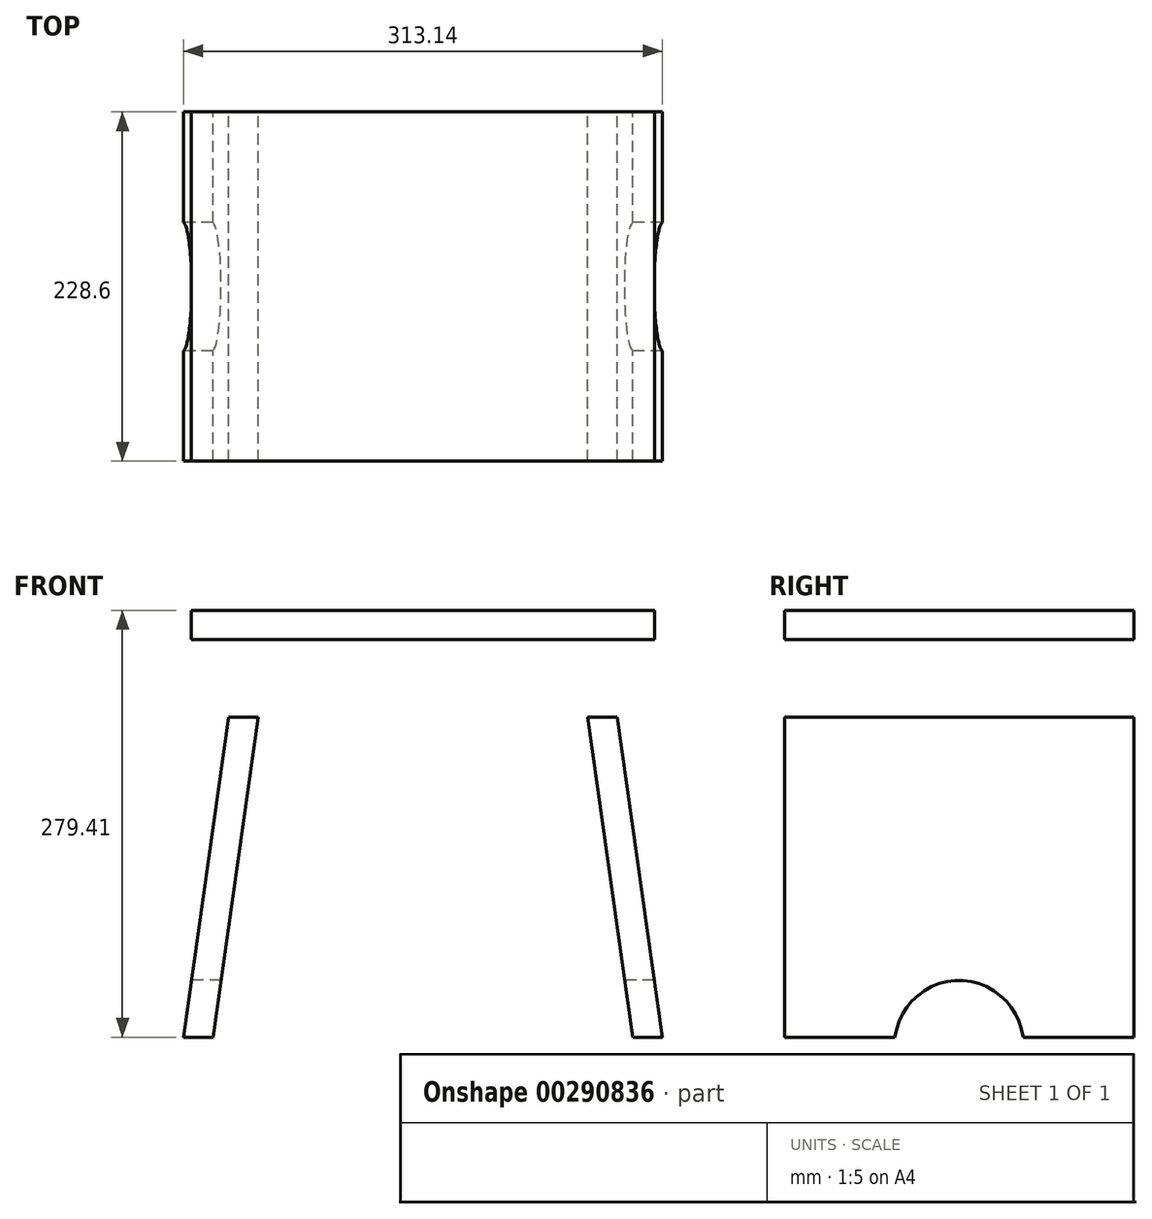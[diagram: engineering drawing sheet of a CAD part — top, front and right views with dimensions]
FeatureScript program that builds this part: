
annotation { "Feature Type Name" : "Feature", "Feature Type Description" : "" }
export const myFeature = defineFeature(function(context is Context, id is Id, definition is map)
    precondition{}
    {
        {
            var Q0;
            Q0=qCreatedBy(makeId("Front.planeOp"),FACE);
            var sketch = newSketch(context, id + "F0", { "sketchPlane" : qUnion([Q0])});
            skLineSegment(sketch, "E0.bottom", {"start": v(-151.6, 9.53) * mm, "end": v(151.6, 9.53) * mm});
            skLineSegment(sketch, "E0.top", {"start": v(-151.6, -9.53) * mm, "end": v(151.6, -9.53) * mm});
            skLineSegment(sketch, "E0.left", {"start": v(-151.6, 9.53) * mm, "end": v(-151.6, -9.53) * mm});
            skLineSegment(sketch, "E0.right", {"start": v(151.6, 9.53) * mm, "end": v(151.6, -9.53) * mm});
            skPoint(sketch, "E0.middle", {"position": v(0, 0) * mm});
            skLineSegment(sketch, "E1", {"start": v(151.6, -9.52) * mm, "end": v(151.6, -60.33) * mm});
            skLineSegment(sketch, "E2", {"start": v(-151.6, -60.33) * mm, "end": v(-151.6, -9.52) * mm});
            skLineSegment(sketch, "E3", {"start": v(-119.86, -9.52) * mm, "end": v(-156.57, -269.88) * mm});
            skLineSegment(sketch, "E4", {"start": v(-156.57, -269.88) * mm, "end": v(-137.33, -269.88) * mm});
            skLineSegment(sketch, "E5", {"start": v(-137.33, -269.88) * mm, "end": v(-100.62, -9.52) * mm});
            skLineSegment(sketch, "E6", {"start": v(-119.86, -9.53) * mm, "end": v(-100.62, -9.53) * mm});
            skLineSegment(sketch, "E7.MirrorCS", {"start": v(119.86, -9.53) * mm, "end": v(100.62, -9.53) * mm});
            skLineSegment(sketch, "E8.MirrorCS", {"start": v(119.86, -9.52) * mm, "end": v(156.57, -269.88) * mm});
            skLineSegment(sketch, "E9.MirrorCS", {"start": v(137.33, -269.88) * mm, "end": v(100.62, -9.52) * mm});
            skLineSegment(sketch, "E10.MirrorCS", {"start": v(156.57, -269.88) * mm, "end": v(137.33, -269.88) * mm});
            skLineSegment(sketch, "E11", {"start": v(-151.6, -60.33) * mm, "end": v(151.6, -60.33) * mm});
            skLineSegment(sketch, "E12", {"start": v(-141.9, -9.52) * mm, "end": v(-134.76, -60.33) * mm});
            skLineSegment(sketch, "E13.MirrorCS", {"start": v(141.9, -9.52) * mm, "end": v(134.76, -60.33) * mm});
            skSolve(sketch);
        }
        {
            var Q0;
            Q0=makeQuery(id+"F0.imprint","IMPRINT",FACE,{"disambiguationData":[TD([[makeQuery(id+"F0.imprint","IMPRINT",EDGE,{"derivedFrom":sQuery(id+"F0.wireOp",EDGE,"E0.bottom")}),-1.0]])]});
            extrude(context, id + "F1", {"entities" : qUnion([Q0]), "endBound" : BoundingType.SYMMETRIC, "depth" : 228.6 * mm});
        }
        {
            var Q0;
            {var subQ0=sQuery(id+"F0.wireOp",EDGE,"E6");Q0=makeQuery(id+"F0.imprint","IMPRINT",FACE,{"disambiguationData":[TD([[makeQuery(id+"F0.imprint","IMPRINT",EDGE,{"derivedFrom":subQ0}),-1.0]])]});}
            var Q1;
            {var subQ0=sQuery(id+"F0.wireOp",EDGE,"E4");Q1=makeQuery(id+"F0.imprint","IMPRINT",FACE,{"disambiguationData":[TD([[makeQuery(id+"F0.imprint","IMPRINT",EDGE,{"derivedFrom":subQ0}),1.0]])]});}
            var Q2;
            {var subQ0=sQuery(id+"F0.wireOp",EDGE,"E7.MirrorCS");Q2=makeQuery(id+"F0.imprint","IMPRINT",FACE,{"disambiguationData":[TD([[makeQuery(id+"F0.imprint","IMPRINT",EDGE,{"derivedFrom":subQ0}),1.0]])]});}
            var Q3;
            {var subQ0=sQuery(id+"F0.wireOp",EDGE,"E10.MirrorCS");Q3=makeQuery(id+"F0.imprint","IMPRINT",FACE,{"disambiguationData":[TD([[makeQuery(id+"F0.imprint","IMPRINT",EDGE,{"derivedFrom":subQ0}),-1.0]])]});}
            extrude(context, id + "F2", {"entities" : qUnion([Q0, Q1, Q2, Q3]), "endBound" : BoundingType.SYMMETRIC, "depth" : 228.6 * mm});
        }
        {
            var Q0;
            Q0=qCreatedBy(makeId("Right.planeOp"),FACE);
            var sketch = newSketch(context, id + "F3", { "sketchPlane" : qUnion([Q0])});
            skLineSegment(sketch, "E14.0.0", {"start": v(114.3, -269.88) * mm, "end": v(114.3, -9.53) * mm});
            skLineSegment(sketch, "E14.0.1", {"start": v(114.3, -9.53) * mm, "end": v(-114.3, -9.53) * mm});
            skLineSegment(sketch, "E14.0.2", {"start": v(-114.3, -9.53) * mm, "end": v(-114.3, -269.88) * mm});
            skLineSegment(sketch, "E14.0.3", {"start": v(-114.3, -269.88) * mm, "end": v(114.3, -269.88) * mm});
            skLineSegment(sketch, "E15", {"start": v(-114.3, -9.52) * mm, "end": v(114.3, -9.53) * mm});
            skLineSegment(sketch, "E16", {"start": v(114.3, -269.88) * mm, "end": v(-114.3, -269.88) * mm});
            skLineSegment(sketch, "E17", {"start": v(-114.3, -269.88) * mm, "end": v(-114.3, -9.53) * mm});
            skLineSegment(sketch, "E18", {"start": v(114.3, -9.53) * mm, "end": v(114.3, -269.88) * mm});
            skLineSegment(sketch, "E19", {"start": v(-114.3, -269.88) * mm, "end": v(-77.71, -9.53) * mm});
            skLineSegment(sketch, "E20.MirrorCS", {"start": v(114.3, -269.88) * mm, "end": v(77.71, -9.52) * mm});
            skPoint(sketch, "E21", {"position": v(0, -269.88) * mm});
            skPoint(sketch, "E22", {"position": v(-41.97, -269.88) * mm});
            skPoint(sketch, "E23.MirrorP", {"position": v(41.97, -269.88) * mm});
            skArc(sketch, "E24", {"start": v(41.97, -269.88) * mm, "mid": v(0, -232.61) * mm, "end": v(-41.97, -269.88) * mm});
            skSolve(sketch);
        }
        {
            var Q0;
            {var subQ0=sQuery(id+"F3.wireOp",EDGE,"E17");Q0=makeQuery(id+"F3.imprint","IMPRINT",FACE,{"disambiguationData":[TD([[makeQuery(id+"F3.imprint","IMPRINT",EDGE,{"derivedFrom":subQ0}),-1.0]])]});}
            var Q1;
            {var subQ0=sQuery(id+"F3.wireOp",EDGE,"E24");Q1=makeQuery(id+"F3.imprint","IMPRINT",FACE,{"disambiguationData":[TD([[makeQuery(id+"F3.imprint","IMPRINT",EDGE,{"derivedFrom":subQ0}),1.0]])]});}
            var Q2;
            {var subQ0=sQuery(id+"F3.wireOp",EDGE,"E18");Q2=makeQuery(id+"F3.imprint","IMPRINT",FACE,{"disambiguationData":[TD([[makeQuery(id+"F3.imprint","IMPRINT",EDGE,{"derivedFrom":subQ0}),-1.0]])]});}
            extrude(context, id + "F4", {"entities" : qUnion([Q0, Q1, Q2]), "operationType" : NewBodyOperationType.REMOVE, "endBound" : BoundingType.SYMMETRIC, "depth" : 381 * mm});
        }
        {
            var Q0;
            Q0=qCreatedBy(makeId("Right.planeOp"),FACE);
            var sketch = newSketch(context, id + "F5", { "sketchPlane" : qUnion([Q0])});
            skLineSegment(sketch, "E25", {"start": v(-71.3, -9.52) * mm, "end": v(-78.44, -60.33) * mm});
            skLineSegment(sketch, "E26", {"start": v(-78.44, -60.33) * mm, "end": v(-97.67, -60.33) * mm});
            skLineSegment(sketch, "E27", {"start": v(-97.67, -60.33) * mm, "end": v(-90.54, -9.52) * mm});
            skLineSegment(sketch, "E28", {"start": v(-90.54, -9.53) * mm, "end": v(-71.3, -9.52) * mm});
            skLineSegment(sketch, "E29.MirrorCS", {"start": v(71.3, -9.52) * mm, "end": v(78.44, -60.33) * mm});
            skLineSegment(sketch, "E30.MirrorCS", {"start": v(90.54, -9.52) * mm, "end": v(71.3, -9.52) * mm});
            skLineSegment(sketch, "E31.MirrorCS", {"start": v(97.67, -60.33) * mm, "end": v(90.54, -9.52) * mm});
            skLineSegment(sketch, "E32.MirrorCS", {"start": v(78.44, -60.32) * mm, "end": v(97.67, -60.32) * mm});
            skLineSegment(sketch, "E33.0.0", {"start": v(-77.71, -9.52) * mm, "end": v(-114.3, -269.88) * mm, "construction": true});
            skLineSegment(sketch, "E33.0.1", {"start": v(-114.3, -269.88) * mm, "end": v(-41.97, -269.88) * mm, "construction": true});
            skArc(sketch, "E33.0.2", {"start": v(41.97, -269.88) * mm, "mid": v(0, -232.61) * mm, "end": v(-41.97, -269.88) * mm, "construction": true});
            skLineSegment(sketch, "E33.0.3", {"start": v(41.97, -269.88) * mm, "end": v(114.3, -269.88) * mm, "construction": true});
            skLineSegment(sketch, "E33.0.4", {"start": v(114.3, -269.88) * mm, "end": v(77.71, -9.52) * mm, "construction": true});
            skLineSegment(sketch, "E33.0.5", {"start": v(77.71, -9.53) * mm, "end": v(-77.71, -9.53) * mm, "construction": true});
            skLineSegment(sketch, "E34", {"start": v(-78.44, -60.33) * mm, "end": v(0, -60.33) * mm});
            skSolve(sketch);
        }
        {
            var Q0;
            Q0=makeQuery(id+"F5.imprint","IMPRINT",FACE,{"disambiguationData":[TD([[makeQuery(id+"F5.imprint","IMPRINT",EDGE,{"derivedFrom":sQuery(id+"F5.wireOp",EDGE,"E25")}),-1.0]])]});
            var Q1;
            Q1=makeQuery(id+"F5.imprint","IMPRINT",FACE,{"disambiguationData":[TD([[makeQuery(id+"F5.imprint","IMPRINT",EDGE,{"derivedFrom":sQuery(id+"F5.wireOp",EDGE,"E29.MirrorCS")}),1.0]])]});
            extrude(context, id + "F6", {"entities" : qUnion([Q0, Q1]), "endBound" : BoundingType.SYMMETRIC, "depth" : 304.8 * mm});
        }
        {
            var Q0;
            Q0=makeQuery(id+"F2.opExtrude","SWEPT_BODY",BODY,{"disambiguationData":[OSD([sQuery(id+"F0.wireOp",EDGE,"E7.MirrorCS"),sQuery(id+"F0.wireOp",EDGE,"E8.MirrorCS"),sQuery(id+"F0.wireOp",EDGE,"E9.MirrorCS"),sQuery(id+"F0.wireOp",EDGE,"E10.MirrorCS")])]});
            var Q1;
            Q1=makeQuery(id+"F2.opExtrude","SWEPT_BODY",BODY,{"disambiguationData":[OSD([sQuery(id+"F0.wireOp",EDGE,"E3"),sQuery(id+"F0.wireOp",EDGE,"E4"),sQuery(id+"F0.wireOp",EDGE,"E5"),sQuery(id+"F0.wireOp",EDGE,"E6")])]});
            var Q2;
            Q2=makeQuery(id+"F6.opExtrude","SWEPT_BODY",BODY,{"disambiguationData":[OSD([sQuery(id+"F5.wireOp",EDGE,"E25"),sQuery(id+"F5.wireOp",EDGE,"E26"),sQuery(id+"F5.wireOp",EDGE,"E27"),sQuery(id+"F5.wireOp",EDGE,"E28")])]});
            var Q3;
            Q3=makeQuery(id+"F6.opExtrude","SWEPT_BODY",BODY,{"disambiguationData":[OSD([sQuery(id+"F5.wireOp",EDGE,"E29.MirrorCS"),sQuery(id+"F5.wireOp",EDGE,"E30.MirrorCS"),sQuery(id+"F5.wireOp",EDGE,"E31.MirrorCS"),sQuery(id+"F5.wireOp",EDGE,"E32.MirrorCS")])]});
            booleanBodies(context, id + "F7", {"operationType" : BooleanOperationType.SUBTRACTION, "tools" : qUnion([Q0, Q1]), "targets" : qUnion([Q2, Q3]), "keepTools" : true});
        }
        {
            var Q0;
            {var subQ0=sQuery(id+"F0.wireOp",EDGE,"E2");Q0=makeQuery(id+"F0.imprint","IMPRINT",FACE,{"disambiguationData":[TD([[makeQuery(id+"F0.imprint","IMPRINT",EDGE,{"derivedFrom":subQ0}),-1.0]])]});}
            var Q1;
            {var subQ0=sQuery(id+"F0.wireOp",EDGE,"E1");Q1=makeQuery(id+"F0.imprint","IMPRINT",FACE,{"disambiguationData":[TD([[makeQuery(id+"F0.imprint","IMPRINT",EDGE,{"derivedFrom":subQ0}),-1.0]])]});}
            extrude(context, id + "F8", {"entities" : qUnion([Q0, Q1]), "operationType" : NewBodyOperationType.REMOVE, "endBound" : BoundingType.SYMMETRIC, "oppositeDirection" : true, "depth" : 254 * mm});
        }
        {
            var Q0;
            Q0=makeQuery(id+"F8.boolean.opBoolean","SPLIT",BODY,{"disambiguationData":[OD(0.0)],"derivedFrom":makeQuery(id+"F6.opExtrude","SWEPT_BODY",BODY,{"disambiguationData":[OSD([sQuery(id+"F5.wireOp",EDGE,"E25"),sQuery(id+"F5.wireOp",EDGE,"E26"),sQuery(id+"F5.wireOp",EDGE,"E27"),sQuery(id+"F5.wireOp",EDGE,"E28")])]})});
            var Q1;
            Q1=makeQuery(id+"F8.boolean.opBoolean","SPLIT",BODY,{"disambiguationData":[OD(1.0)],"derivedFrom":makeQuery(id+"F6.opExtrude","SWEPT_BODY",BODY,{"disambiguationData":[OSD([sQuery(id+"F5.wireOp",EDGE,"E25"),sQuery(id+"F5.wireOp",EDGE,"E26"),sQuery(id+"F5.wireOp",EDGE,"E27"),sQuery(id+"F5.wireOp",EDGE,"E28")])]})});
            deleteBodies(context, id + "F9", {"entities" : qUnion([Q0, Q1])});
        }
        {
            var Q0;
            Q0=makeQuery(id+"F8.boolean.opBoolean","SPLIT",BODY,{"disambiguationData":[OD(0.0)],"derivedFrom":makeQuery(id+"F6.opExtrude","SWEPT_BODY",BODY,{"disambiguationData":[OSD([sQuery(id+"F5.wireOp",EDGE,"E29.MirrorCS"),sQuery(id+"F5.wireOp",EDGE,"E30.MirrorCS"),sQuery(id+"F5.wireOp",EDGE,"E31.MirrorCS"),sQuery(id+"F5.wireOp",EDGE,"E32.MirrorCS")])]})});
            var Q1;
            Q1=makeQuery(id+"F8.boolean.opBoolean","SPLIT",BODY,{"disambiguationData":[OD(1.0)],"derivedFrom":makeQuery(id+"F6.opExtrude","SWEPT_BODY",BODY,{"disambiguationData":[OSD([sQuery(id+"F5.wireOp",EDGE,"E29.MirrorCS"),sQuery(id+"F5.wireOp",EDGE,"E30.MirrorCS"),sQuery(id+"F5.wireOp",EDGE,"E31.MirrorCS"),sQuery(id+"F5.wireOp",EDGE,"E32.MirrorCS")])]})});
            deleteBodies(context, id + "F10", {"entities" : qUnion([Q0, Q1])});
        }
    });
